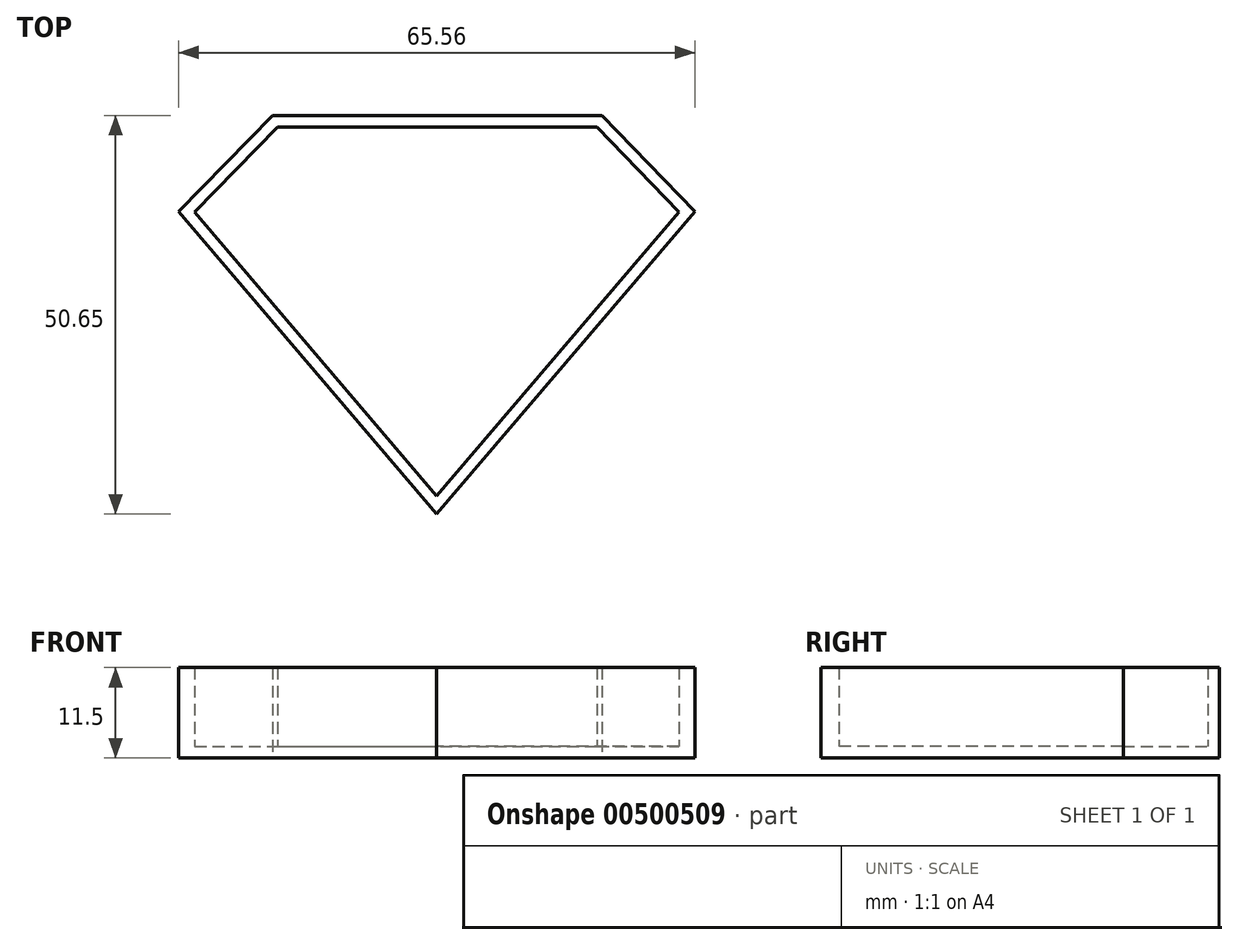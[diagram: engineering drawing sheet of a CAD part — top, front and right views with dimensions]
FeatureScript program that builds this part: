
annotation { "Feature Type Name" : "Feature", "Feature Type Description" : "" }
export const myFeature = defineFeature(function(context is Context, id is Id, definition is map)
    precondition{}
    {
        {
            var Q0;
            Q0=qCreatedBy(makeId("Top.planeOp"),FACE);
            var sketch = newSketch(context, id + "F0", { "sketchPlane" : qUnion([Q0])});
            skLineSegment(sketch, "E0", {"start": v(-20.25, 19.13) * mm, "end": v(20.36, 19.13) * mm});
            skLineSegment(sketch, "E1", {"start": v(20.36, 19.13) * mm, "end": v(30.75, 8.34) * mm});
            skLineSegment(sketch, "E2", {"start": v(30.75, 8.34) * mm, "end": v(0, -27.7) * mm});
            skLineSegment(sketch, "E3", {"start": v(0, 16.23) * mm, "end": v(19.01, 16.23) * mm});
            skLineSegment(sketch, "E4", {"start": v(19.01, 16.23) * mm, "end": v(26.4, 8.42) * mm});
            skLineSegment(sketch, "E5", {"start": v(26.4, 8.42) * mm, "end": v(0, -22.32) * mm});
            skLineSegment(sketch, "E6.MirrorCS", {"start": v(-26.4, 8.42) * mm, "end": v(0, -22.32) * mm});
            skLineSegment(sketch, "E7.MirrorCS", {"start": v(0, 16.23) * mm, "end": v(-19.01, 16.23) * mm});
            skLineSegment(sketch, "E8.MirrorCS", {"start": v(-30.75, 8.34) * mm, "end": v(0, -27.7) * mm});
            skLineSegment(sketch, "E9", {"start": v(-30.75, 8.34) * mm, "end": v(-26.4, 8.42) * mm});
            skLineSegment(sketch, "E10", {"start": v(-20.25, 19.13) * mm, "end": v(-19.01, 16.23) * mm});
            skLineSegment(sketch, "E11", {"start": v(20.36, 19.13) * mm, "end": v(19.01, 16.23) * mm});
            skLineSegment(sketch, "E12", {"start": v(30.75, 8.34) * mm, "end": v(26.4, 8.42) * mm});
            skLineSegment(sketch, "E13", {"start": v(0, -22.32) * mm, "end": v(0, -27.7) * mm});
            skLineSegment(sketch, "E14", {"start": v(-26.4, 8.42) * mm, "end": v(-19.01, 16.23) * mm});
            skLineSegment(sketch, "E15", {"start": v(-30.75, 8.34) * mm, "end": v(-20.25, 19.13) * mm});
            skSolve(sketch);
        }
        {
            var Q0;
            Q0=makeQuery(id+"F0.imprint","IMPRINT",FACE,{"disambiguationData":[TD([[makeQuery(id+"F0.imprint","IMPRINT",EDGE,{"derivedFrom":sQuery(id+"F0.wireOp",EDGE,"E3")}),-1.0]])]});
            extrude(context, id + "F1", {"entities" : qUnion([Q0]), "depth" : 10 * mm});
        }
        {
            var Q0;
            Q0=makeQuery(id+"F0.imprint","IMPRINT",FACE,{"disambiguationData":[TD([[makeQuery(id+"F0.imprint","IMPRINT",EDGE,{"derivedFrom":sQuery(id+"F0.wireOp",EDGE,"E9")}),1.0]])]});
            var Q1;
            Q1=makeQuery(id+"F0.imprint","IMPRINT",FACE,{"disambiguationData":[TD([[makeQuery(id+"F0.imprint","IMPRINT",EDGE,{"derivedFrom":sQuery(id+"F0.wireOp",EDGE,"E0")}),-1.0]])]});
            var Q2;
            Q2=makeQuery(id+"F0.imprint","IMPRINT",FACE,{"disambiguationData":[TD([[makeQuery(id+"F0.imprint","IMPRINT",EDGE,{"derivedFrom":sQuery(id+"F0.wireOp",EDGE,"E1")}),-1.0]])]});
            var Q3;
            Q3=makeQuery(id+"F0.imprint","IMPRINT",FACE,{"disambiguationData":[TD([[makeQuery(id+"F0.imprint","IMPRINT",EDGE,{"derivedFrom":sQuery(id+"F0.wireOp",EDGE,"E2")}),-1.0]])]});
            var Q4;
            Q4=makeQuery(id+"F0.imprint","IMPRINT",FACE,{"disambiguationData":[TD([[makeQuery(id+"F0.imprint","IMPRINT",EDGE,{"derivedFrom":sQuery(id+"F0.wireOp",EDGE,"E6.MirrorCS")}),-1.0]])]});
            extrude(context, id + "F2", {"entities" : qUnion([Q0, Q1, Q2, Q3, Q4]), "operationType" : NewBodyOperationType.ADD, "depth" : 10 * mm});
        }
        {
            var Q0;
            {var subQ0=sQuery(id+"F0.wireOp",EDGE,"E14");var subQ1=sQuery(id+"F0.wireOp",EDGE,"E7.MirrorCS");var subQ2=sQuery(id+"F0.wireOp",EDGE,"E6.MirrorCS");var subQ3=sQuery(id+"F0.wireOp",EDGE,"E5");var subQ4=sQuery(id+"F0.wireOp",EDGE,"E4");var subQ5=sQuery(id+"F0.wireOp",EDGE,"E3");Q0=makeQuery(id+"F2.boolean.opBoolean","MERGE",FACE,{"derivedFrom":[makeQuery(id+"F1.opExtrude","CAP_FACE",FACE,{"disambiguationData":[OSD([subQ5,subQ4,subQ3,subQ2,subQ1,subQ0])],"isStart":false}),makeQuery(id+"F2.opExtrude","CAP_FACE",FACE,{"disambiguationData":[OSD([sQuery(id+"F0.wireOp",EDGE,"E0"),sQuery(id+"F0.wireOp",EDGE,"E1"),sQuery(id+"F0.wireOp",EDGE,"E2"),subQ5,subQ4,subQ3,subQ2,subQ1,sQuery(id+"F0.wireOp",EDGE,"E8.MirrorCS"),subQ0,sQuery(id+"F0.wireOp",EDGE,"E15")])],"isStart":false})]});}
            shell(context, id + "F3", {"entities" : qUnion([Q0]), "thickness" : 1.5 * mm, "oppositeDirection" : true});
        }
        {
            var Q0;
            {var subQ0=sQuery(id+"F0.wireOp",EDGE,"E14");var subQ1=sQuery(id+"F0.wireOp",EDGE,"E7.MirrorCS");var subQ2=sQuery(id+"F0.wireOp",EDGE,"E6.MirrorCS");var subQ3=sQuery(id+"F0.wireOp",EDGE,"E5");var subQ4=sQuery(id+"F0.wireOp",EDGE,"E4");var subQ5=sQuery(id+"F0.wireOp",EDGE,"E3");Q0=makeQuery(id+"F2.boolean.opBoolean","MERGE",FACE,{"derivedFrom":[makeQuery(id+"F1.opExtrude","CAP_FACE",FACE,{"disambiguationData":[OSD([subQ5,subQ4,subQ3,subQ2,subQ1,subQ0])],"isStart":true}),makeQuery(id+"F2.opExtrude","CAP_FACE",FACE,{"disambiguationData":[OSD([sQuery(id+"F0.wireOp",EDGE,"E0"),sQuery(id+"F0.wireOp",EDGE,"E1"),sQuery(id+"F0.wireOp",EDGE,"E2"),subQ5,subQ4,subQ3,subQ2,subQ1,sQuery(id+"F0.wireOp",EDGE,"E8.MirrorCS"),subQ0,sQuery(id+"F0.wireOp",EDGE,"E15")])],"isStart":true})]});}
            var sketch = newSketch(context, id + "F4", { "sketchPlane" : qUnion([Q0])});
            skCircle(sketch, "E16", {"center": v(0, 0) * mm, "radius": 5.88 * mm});
            skSolve(sketch);
        }
        {
            var Q0;
            Q0 = qSketchRegion(id + "F4", true);
            extrude(context, id + "F5", {"entities" : qUnion([Q0]), "operationType" : NewBodyOperationType.REMOVE, "depth" : 25.4 * mm});
        }
    });
